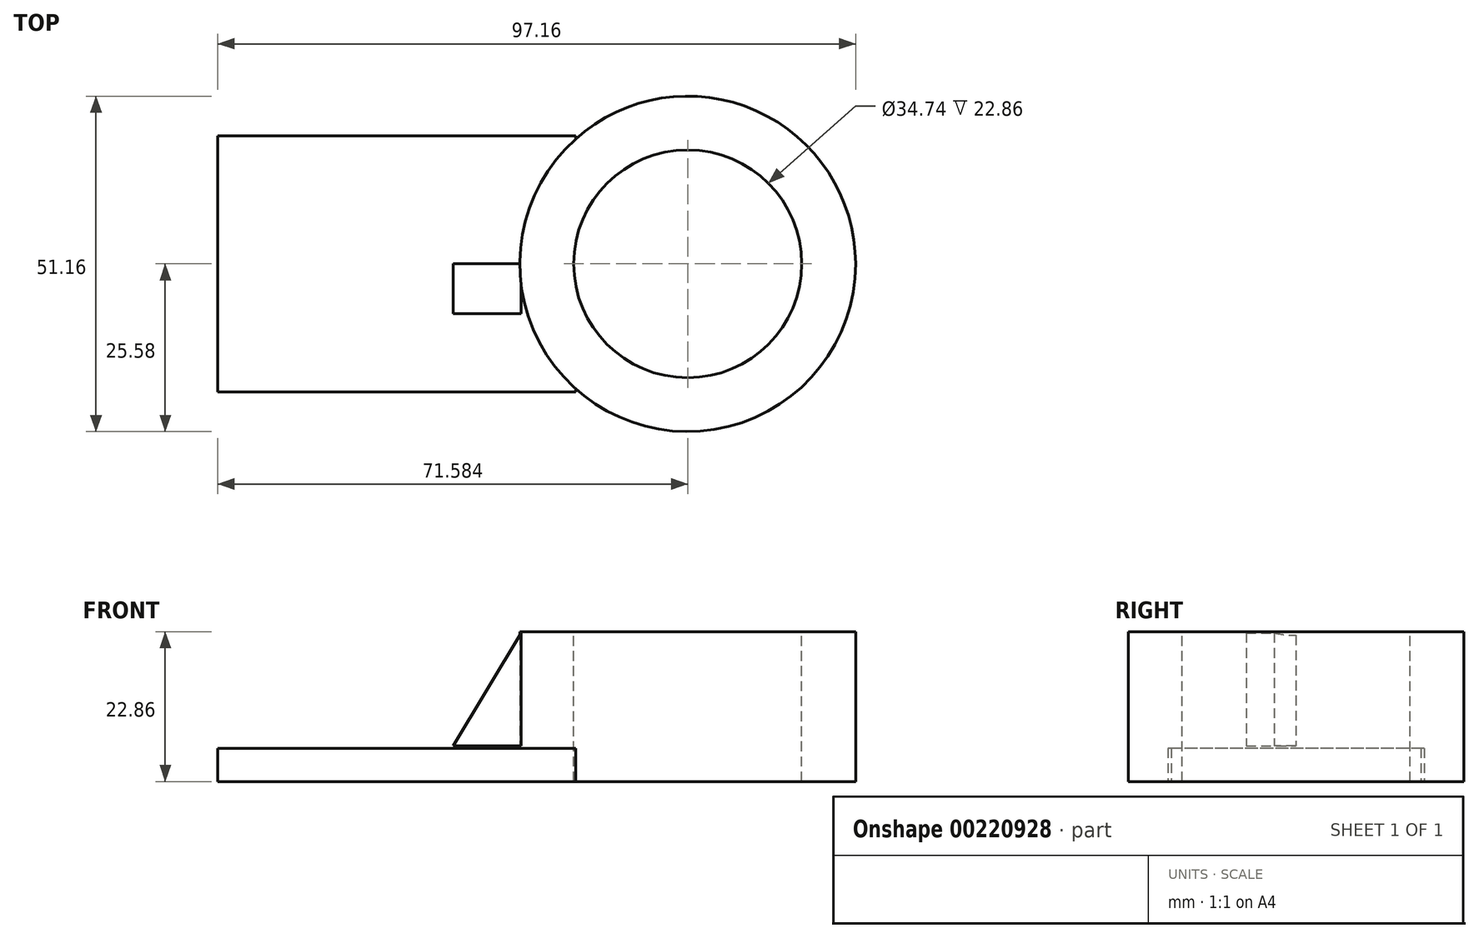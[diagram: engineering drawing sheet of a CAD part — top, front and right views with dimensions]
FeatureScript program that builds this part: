
annotation { "Feature Type Name" : "Feature", "Feature Type Description" : "" }
export const myFeature = defineFeature(function(context is Context, id is Id, definition is map)
    precondition{}
    {
        {
            var Q0;
            Q0=qCreatedBy(makeId("Top.planeOp"),FACE);
            var sketch = newSketch(context, id + "F0", { "sketchPlane" : qUnion([Q0])});
            skLineSegment(sketch, "E0.bottom", {"start": v(27.25, 19.51) * mm, "end": v(-27.25, 19.51) * mm});
            skLineSegment(sketch, "E0.top", {"start": v(27.25, -19.51) * mm, "end": v(-27.25, -19.51) * mm});
            skLineSegment(sketch, "E0.left", {"start": v(27.25, 19.51) * mm, "end": v(27.25, -19.51) * mm});
            skLineSegment(sketch, "E0.right", {"start": v(-27.25, 19.51) * mm, "end": v(-27.25, -19.51) * mm});
            skPoint(sketch, "E0.middle", {"position": v(0, 0) * mm});
            skSolve(sketch);
        }
        {
            var Q0;
            Q0=makeQuery(id+"F0.imprint","IMPRINT",FACE,{"disambiguationData":[TD([[makeQuery(id+"F0.imprint","IMPRINT",EDGE,{"derivedFrom":sQuery(id+"F0.wireOp",EDGE,"E0.bottom")}),1.0]])]});
            extrude(context, id + "F1", {"entities" : qUnion([Q0]), "depth" : 5.08 * mm});
        }
        {
            var Q0;
            Q0=makeQuery(id+"F1.opExtrude","CAP_FACE",FACE,{"disambiguationData":[OSD([sQuery(id+"F0.wireOp",EDGE,"E0.bottom"),sQuery(id+"F0.wireOp",EDGE,"E0.top"),sQuery(id+"F0.wireOp",EDGE,"E0.left"),sQuery(id+"F0.wireOp",EDGE,"E0.right")])],"isStart":false});
            var sketch = newSketch(context, id + "F2", { "sketchPlane" : qUnion([Q0])});
            skCircle(sketch, "E1", {"center": v(44.33, 0) * mm, "radius": 25.58 * mm});
            skSolve(sketch);
        }
        {
            var Q0;
            {var subQ0=sQuery(id+"F2.wireOp",EDGE,"E1");var subQ1=makeQuery(id+"F1.opExtrude","CAP_EDGE",EDGE,{"disambiguationData":[OSD([sQuery(id+"F0.wireOp",EDGE,"E0.left")])],"isStart":false});var subQ2=makeQuery(id+"F2.imprint","INTERSECT",VERTEX,{"disambiguationData":[OD(0.0)],"derivedFrom":[subQ1,subQ0]});Q0=makeQuery(id+"F2.imprint","IMPRINT",FACE,{"disambiguationData":[TD([[makeQuery(id+"F2.imprint","IMPRINT",EDGE,{"disambiguationData":[TD([[subQ2,-1.0]])],"derivedFrom":subQ0}),1.0]])]});}
            var Q1;
            {var subQ0=sQuery(id+"F2.wireOp",EDGE,"E1");var subQ1=makeQuery(id+"F1.opExtrude","CAP_EDGE",EDGE,{"disambiguationData":[OSD([sQuery(id+"F0.wireOp",EDGE,"E0.left")])],"isStart":false});var subQ2=makeQuery(id+"F2.imprint","INTERSECT",VERTEX,{"disambiguationData":[OD(0.0)],"derivedFrom":[subQ1,subQ0]});Q1=makeQuery(id+"F2.imprint","IMPRINT",FACE,{"disambiguationData":[TD([[makeQuery(id+"F2.imprint","IMPRINT",EDGE,{"disambiguationData":[TD([[subQ2,1.0]])],"derivedFrom":subQ0}),1.0]])]});}
            extrude(context, id + "F3", {"entities" : qUnion([Q0, Q1]), "operationType" : NewBodyOperationType.ADD, "endBound" : BoundingType.SYMMETRIC, "depth" : 25.4 * mm});
        }
        {
            var Q0;
            Q0=qCreatedBy(makeId("Front.planeOp"),FACE);
            var sketch = newSketch(context, id + "F4", { "sketchPlane" : qUnion([Q0])});
            skLineSegment(sketch, "E2.bottom", {"start": v(46.64, -15.82) * mm, "end": v(18.47, -15.82) * mm});
            skLineSegment(sketch, "E2.top", {"start": v(46.64, 0) * mm, "end": v(18.47, 0) * mm});
            skLineSegment(sketch, "E2.left", {"start": v(46.64, -15.82) * mm, "end": v(46.64, 0) * mm});
            skLineSegment(sketch, "E2.right", {"start": v(18.47, -15.82) * mm, "end": v(18.47, 0) * mm});
            skLineSegment(sketch, "E3.bottom", {"start": v(46.64, 0) * mm, "end": v(70.2, 0) * mm});
            skLineSegment(sketch, "E3.top", {"start": v(46.64, -15.82) * mm, "end": v(70.2, -15.82) * mm});
            skLineSegment(sketch, "E3.left", {"start": v(46.64, 0) * mm, "end": v(46.64, -15.82) * mm});
            skLineSegment(sketch, "E3.right", {"start": v(70.2, 0) * mm, "end": v(70.2, -15.82) * mm});
            skSolve(sketch);
        }
        {
            var Q0;
            Q0=makeQuery(id+"F4.imprint","IMPRINT",FACE,{"disambiguationData":[TD([[makeQuery(id+"F4.imprint","IMPRINT",EDGE,{"derivedFrom":sQuery(id+"F4.wireOp",EDGE,"E2.bottom")}),-1.0]])]});
            var Q1;
            Q1=makeQuery(id+"F4.imprint","IMPRINT",FACE,{"disambiguationData":[TD([[makeQuery(id+"F4.imprint","IMPRINT",EDGE,{"derivedFrom":sQuery(id+"F4.wireOp",EDGE,"E3.bottom")}),-1.0]])]});
            extrude(context, id + "F5", {"entities" : qUnion([Q0, Q1]), "operationType" : NewBodyOperationType.REMOVE, "endBound" : BoundingType.THROUGH_ALL, "oppositeDirection" : true, "depth" : 25.4 * mm});
        }
        {
            var Q0;
            Q0=qCreatedBy(makeId("Front.planeOp"),FACE);
            var sketch = newSketch(context, id + "F6", { "sketchPlane" : qUnion([Q0])});
            skLineSegment(sketch, "E4.bottom", {"start": v(18.7, 0) * mm, "end": v(76.43, 0) * mm});
            skLineSegment(sketch, "E4.top", {"start": v(18.7, -25.63) * mm, "end": v(76.43, -25.63) * mm});
            skLineSegment(sketch, "E4.left", {"start": v(18.7, 0) * mm, "end": v(18.7, -25.63) * mm});
            skLineSegment(sketch, "E4.right", {"start": v(76.43, 0) * mm, "end": v(76.43, -25.63) * mm});
            skPoint(sketch, "E4.middle", {"position": v(47.57, -12.82) * mm});
            skSolve(sketch);
        }
        {
            var Q0;
            Q0=makeQuery(id+"F6.imprint","IMPRINT",FACE,{"disambiguationData":[TD([[makeQuery(id+"F6.imprint","IMPRINT",EDGE,{"derivedFrom":sQuery(id+"F6.wireOp",EDGE,"E4.bottom")}),-1.0]])]});
            extrude(context, id + "F7", {"entities" : qUnion([Q0]), "operationType" : NewBodyOperationType.REMOVE, "endBound" : BoundingType.THROUGH_ALL, "depth" : 25.4 * mm});
        }
        {
            var Q0;
            Q0=makeQuery(id+"F3.opExtrude","CAP_FACE",FACE,{"disambiguationData":[OSD([sQuery(id+"F2.wireOp",EDGE,"E1")])],"isStart":false});
            var sketch = newSketch(context, id + "F8", { "sketchPlane" : qUnion([Q0])});
            skCircle(sketch, "E5", {"center": v(44.33, 0) * mm, "radius": 17.37 * mm});
            skSolve(sketch);
        }
        {
            var Q0;
            Q0=makeQuery(id+"F8.imprint","IMPRINT",FACE,{"disambiguationData":[TD([[makeQuery(id+"F8.imprint","IMPRINT",EDGE,{"derivedFrom":sQuery(id+"F8.wireOp",EDGE,"E5")}),1.0]])]});
            extrude(context, id + "F9", {"entities" : qUnion([Q0]), "operationType" : NewBodyOperationType.REMOVE, "endBound" : BoundingType.THROUGH_ALL, "oppositeDirection" : true, "depth" : 25.4 * mm});
        }
        {
            var Q0;
            Q0=makeQuery(id+"F3.opExtrude","CAP_FACE",FACE,{"disambiguationData":[OSD([sQuery(id+"F2.wireOp",EDGE,"E1")])],"isStart":false});
            extrude(context, id + "F10", {"entities" : qUnion([Q0]), "operationType" : NewBodyOperationType.ADD, "depth" : 5.08 * mm});
        }
        {
            var Q0;
            Q0=qCreatedBy(makeId("Front.planeOp"),FACE);
            var sketch = newSketch(context, id + "F11", { "sketchPlane" : qUnion([Q0])});
            skLineSegment(sketch, "E6", {"start": v(18.98, 22.66) * mm, "end": v(18.98, 5.42) * mm});
            skLineSegment(sketch, "E7", {"start": v(18.98, 22.66) * mm, "end": v(8.6, 5.42) * mm});
            skLineSegment(sketch, "E8", {"start": v(8.6, 5.42) * mm, "end": v(18.98, 5.42) * mm});
            skSolve(sketch);
        }
        {
            var Q0;
            Q0=makeQuery(id+"F11.imprint","IMPRINT",FACE,{"disambiguationData":[TD([[makeQuery(id+"F11.imprint","IMPRINT",EDGE,{"derivedFrom":sQuery(id+"F11.wireOp",EDGE,"E6")}),-1.0]])]});
            extrude(context, id + "F12", {"entities" : qUnion([Q0]), "operationType" : NewBodyOperationType.ADD, "depth" : 7.62 * mm});
        }
    });
